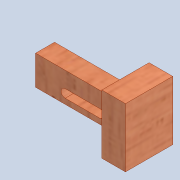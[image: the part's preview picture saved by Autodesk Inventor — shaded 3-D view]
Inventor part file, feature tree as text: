
AUTODESK INVENTOR PART (.ipt)
format: ipt  version: 2020 (Build 240168000, 168)  size: 157,696 bytes
history: native  units: mm
features: extrude x4, sketch x4, fillet x1
ambient origin geometry x8: Origin, YZ Plane, XZ Plane, XY Plane, X Axis, Y Axis, Z Axis, Center Point
bodies: Solid1 (feature_tree)
feature tree (9):
  extrude  "Extrusion1"  Depth=25.0mm
  extrude  "Extrusion5"  Depth=3.5mm
  extrude  "Extrusion6"  Depth=4.0mm
  extrude  "Extrusion7"  Depth=2.0mm
  fillet  "Fillet2"  Radius=15.0mm
  sketch  "Sketch1"  dims[d0=50.0mm d1=25.0mm]
  sketch  "Sketch5"  dims[d2=20.0mm d3=0.0mm d29=3.5mm]
  sketch  "Sketch6"  dims[d30=4.0mm d31=4.0mm]
  sketch  "Sketch7"  dims[d32=20.0mm d33=15.0mm d34=15.0mm d35=0.0mm d36=10.0mm d37=10.0mm d38=0.0mm d40=12.0mm d41=0.0mm d42=2.0mm]
